# Revit family: Faucet-Kitchen-KOHLER-Malleco-K-R562
name_source: partatom
category: Plumbing Fixtures
revit_build: Autodesk Revit 2015 (Build: 20140606_1530(x64)
units: mm (PartAtom-declared; Revit-internal decimal feet)

## types (3) — shared parameters
ADA Compliant = Yes
Assembly Code = D2010
CW Connection = Yes
Cold Water Inlet = Cold Water Inlet
Date Modified = 3/06/2019
Default Elevation = 36"
Description = Pull-down kitchen sink faucet with soap/lotion dispenser
Drain Included = No
Faucet Hole Spacing = 0"
Finish = Kohler-Metal-VS-Vibrant_Stainless
Flow Rate = 2 GPM
HW Connection = Yes
Handle Clearance = 0"
Height = 15 1/2"
Hot Water Inlet = Hot Water Inlet
Length = 9"
Manufacturer = KOHLER Co.
MasterFormat 1995 = 15410
MasterFormat 2004 = 22.41.39
Material = Metal Construction
Model = K-R562-SD-VS
Pressure = 60.00 psi
Product Documentation Link = https://www.us.kohler.com
Product Name = Malleco
Product Page URL = http://www.us.kohler.com
Spout Reach = 9"
URL = https://www.us.kohler.com
Vent Connection = No
Waste Connection = No
Waste Water Outlet = Waste Water Outlet
WaterSense Certified = No
Width = 10 1/2"

## per-type parameters (varying)
| type | Handle  Material |
| White Handle, VS-Vibrant Stainless | Kohler-Silicone-0-White |
| Black Handle, VS-Vibrant Stainless | Kohler-Silicone-7-Black_Black |
| Taupe Handle, VS-Vibrant Stainless | Kohler-Silicone-CM3-Matte_Taupe |

## geometry (parser evidence)
native form markers: Sweep x9
no freeform markers — native parametric forms only
